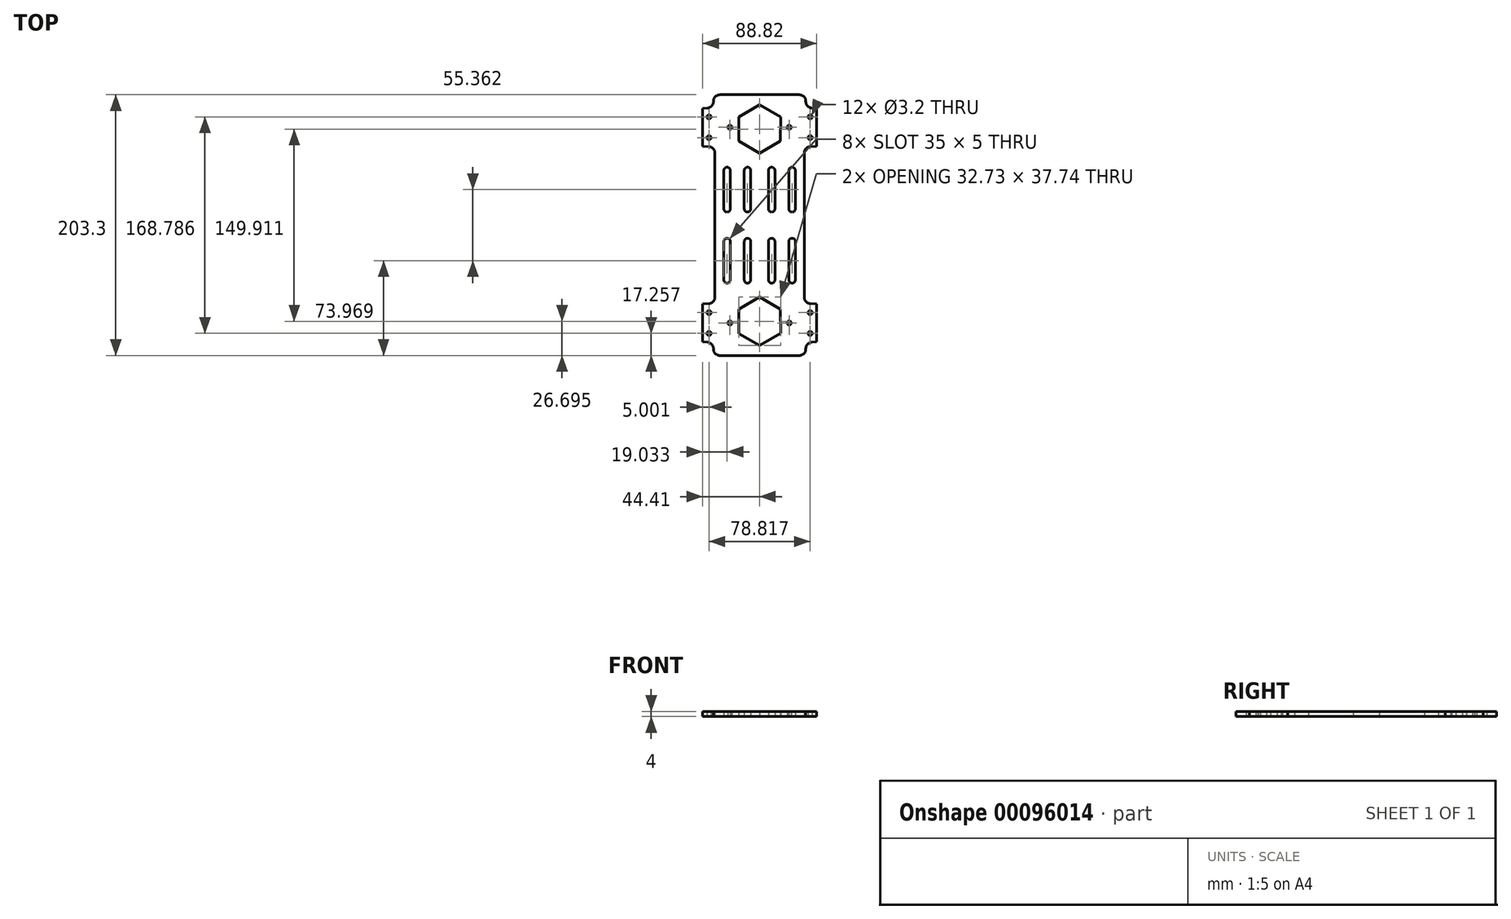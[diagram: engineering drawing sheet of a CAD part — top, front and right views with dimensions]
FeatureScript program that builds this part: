
annotation { "Feature Type Name" : "Feature", "Feature Type Description" : "" }
export const myFeature = defineFeature(function(context is Context, id is Id, definition is map)
    precondition{}
    {
        {
            var Q0;
            Q0=qCreatedBy(makeId("Top.planeOp"),FACE);
            var sketch = newSketch(context, id + "F0", { "sketchPlane" : qUnion([Q0])});
            skCircle(sketch, "E0", {"center": v(-39.4, -84.4) * mm, "radius": 1.6 * mm});
            skCircle(sketch, "E1", {"center": v(-39.4, -68.2) * mm, "radius": 1.6 * mm});
            skCircle(sketch, "E2", {"center": v(-23.11, -76.3) * mm, "radius": 1.6 * mm});
            skLineSegment(sketch, "E3", {"start": v(-39.4, -84.4) * mm, "end": v(-23.11, -76.3) * mm, "construction": true});
            skLineSegment(sketch, "E4", {"start": v(-23.11, -76.3) * mm, "end": v(-39.4, -68.2) * mm, "construction": true});
            skLineSegment(sketch, "E5", {"start": v(-39.4, -84.4) * mm, "end": v(-39.4, -68.2) * mm, "construction": true});
            skLineSegment(sketch, "E6", {"start": v(-44.4, -91.06) * mm, "end": v(-44.4, -61.53) * mm});
            skLineSegment(sketch, "E7", {"start": v(-44.4, -61.53) * mm, "end": v(-39.45, -61.18) * mm});
            skLineSegment(sketch, "E8", {"start": v(-34.8, -56.2) * mm, "end": v(-34.8, 0) * mm});
            skLineSegment(sketch, "E9.MirrorCS", {"start": v(-44.4, -91.06) * mm, "end": v(-40.65, -91.32) * mm});
            skPoint(sketch, "E10.visualSharp", {"position": v(-34.8, -60.85) * mm});
            skArc(sketch, "E10.filletArc", {"start": v(-39.45, -61.18) * mm, "mid": v(-36.14, -59.6) * mm, "end": v(-34.8, -56.2) * mm});
            skLineSegment(sketch, "E11", {"start": v(-36, -96.31) * mm, "end": v(-36, -96.65) * mm});
            skLineSegment(sketch, "E12", {"start": v(-31, -101.65) * mm, "end": v(0, -101.65) * mm});
            skPoint(sketch, "E13.visualSharp", {"position": v(-36, -101.65) * mm});
            skArc(sketch, "E13.filletArc", {"start": v(-36, -96.65) * mm, "mid": v(-34.54, -100.18) * mm, "end": v(-31, -101.65) * mm});
            skPoint(sketch, "E14.visualSharp", {"position": v(-36, -91.65) * mm});
            skArc(sketch, "E14.filletArc", {"start": v(-36, -96.31) * mm, "mid": v(-37.34, -92.9) * mm, "end": v(-40.65, -91.32) * mm});
            skCircle(sketch, "E15.MirrorC", {"center": v(23.11, -76.3) * mm, "radius": 1.6 * mm});
            skCircle(sketch, "E16.MirrorC", {"center": v(39.4, -68.2) * mm, "radius": 1.6 * mm});
            skCircle(sketch, "E17.MirrorC", {"center": v(39.4, -84.4) * mm, "radius": 1.6 * mm});
            skArc(sketch, "E18.MirrorCS", {"start": v(39.45, -61.18) * mm, "mid": v(36.14, -59.6) * mm, "end": v(34.8, -56.2) * mm});
            skLineSegment(sketch, "E19.MirrorCS", {"start": v(44.4, -91.06) * mm, "end": v(40.65, -91.32) * mm});
            skLineSegment(sketch, "E20.MirrorCS", {"start": v(36, -96.31) * mm, "end": v(36, -96.65) * mm});
            skArc(sketch, "E21.MirrorCS", {"start": v(36, -96.31) * mm, "mid": v(37.34, -92.9) * mm, "end": v(40.65, -91.32) * mm});
            skArc(sketch, "E22.MirrorCS", {"start": v(36, -96.65) * mm, "mid": v(34.54, -100.18) * mm, "end": v(31, -101.65) * mm});
            skLineSegment(sketch, "E23.MirrorCS", {"start": v(44.4, -61.53) * mm, "end": v(39.45, -61.18) * mm});
            skLineSegment(sketch, "E24.MirrorCS", {"start": v(39.4, -84.4) * mm, "end": v(39.4, -68.2) * mm, "construction": true});
            skLineSegment(sketch, "E25.MirrorCS", {"start": v(39.4, -84.4) * mm, "end": v(23.11, -76.3) * mm, "construction": true});
            skPoint(sketch, "E26.MirrorP", {"position": v(36, -101.65) * mm});
            skLineSegment(sketch, "E27.MirrorCS", {"start": v(23.11, -76.3) * mm, "end": v(39.4, -68.2) * mm, "construction": true});
            skLineSegment(sketch, "E28.MirrorCS", {"start": v(31, -101.65) * mm, "end": v(0, -101.65) * mm});
            skLineSegment(sketch, "E29.MirrorCS", {"start": v(34.8, -56.2) * mm, "end": v(34.8, 0) * mm});
            skPoint(sketch, "E30.MirrorP", {"position": v(36, -91.65) * mm});
            skPoint(sketch, "E31.MirrorP", {"position": v(34.8, -60.85) * mm});
            skCircle(sketch, "E32.MirrorC", {"center": v(-23.11, 76.3) * mm, "radius": 1.6 * mm});
            skCircle(sketch, "E33.MirrorC", {"center": v(-39.4, 84.4) * mm, "radius": 1.6 * mm});
            skCircle(sketch, "E34.MirrorC", {"center": v(-39.4, 68.2) * mm, "radius": 1.6 * mm});
            skArc(sketch, "E35.MirrorCS", {"start": v(-36, 96.31) * mm, "mid": v(-37.34, 92.9) * mm, "end": v(-40.65, 91.32) * mm});
            skLineSegment(sketch, "E36.MirrorCS", {"start": v(-44.4, 61.53) * mm, "end": v(-39.45, 61.18) * mm});
            skArc(sketch, "E37.MirrorCS", {"start": v(36, 96.65) * mm, "mid": v(34.54, 100.18) * mm, "end": v(31, 101.65) * mm});
            skCircle(sketch, "E38.MirrorC", {"center": v(39.4, 68.2) * mm, "radius": 1.6 * mm});
            skLineSegment(sketch, "E39.MirrorCS", {"start": v(36, 96.31) * mm, "end": v(36, 96.65) * mm});
            skArc(sketch, "E40.MirrorCS", {"start": v(-36, 96.65) * mm, "mid": v(-34.54, 100.18) * mm, "end": v(-31, 101.65) * mm});
            skArc(sketch, "E41.MirrorCS", {"start": v(36, 96.31) * mm, "mid": v(37.34, 92.9) * mm, "end": v(40.65, 91.32) * mm});
            skArc(sketch, "E42.MirrorCS", {"start": v(-39.45, 61.18) * mm, "mid": v(-36.14, 59.6) * mm, "end": v(-34.8, 56.2) * mm});
            skLineSegment(sketch, "E43.MirrorCS", {"start": v(-44.4, 91.06) * mm, "end": v(-40.65, 91.32) * mm});
            skCircle(sketch, "E44.MirrorC", {"center": v(23.11, 76.3) * mm, "radius": 1.6 * mm});
            skLineSegment(sketch, "E45.MirrorCS", {"start": v(-36, 96.31) * mm, "end": v(-36, 96.65) * mm});
            skCircle(sketch, "E46.MirrorC", {"center": v(39.4, 84.4) * mm, "radius": 1.6 * mm});
            skLineSegment(sketch, "E47.MirrorCS", {"start": v(44.4, 91.06) * mm, "end": v(40.65, 91.32) * mm});
            skArc(sketch, "E48.MirrorCS", {"start": v(39.45, 61.18) * mm, "mid": v(36.14, 59.6) * mm, "end": v(34.8, 56.2) * mm});
            skLineSegment(sketch, "E49.MirrorCS", {"start": v(44.4, 61.53) * mm, "end": v(39.45, 61.18) * mm});
            skLineSegment(sketch, "E50.MirrorCS", {"start": v(-39.4, 84.4) * mm, "end": v(-39.4, 68.2) * mm, "construction": true});
            skPoint(sketch, "E51.MirrorP", {"position": v(-34.8, 60.85) * mm});
            skLineSegment(sketch, "E52.MirrorCS", {"start": v(-39.4, 84.4) * mm, "end": v(-23.11, 76.3) * mm, "construction": true});
            skLineSegment(sketch, "E53.MirrorCS", {"start": v(-23.11, 76.3) * mm, "end": v(-39.4, 68.2) * mm, "construction": true});
            skPoint(sketch, "E54.MirrorP", {"position": v(34.8, 60.85) * mm});
            skLineSegment(sketch, "E55.MirrorCS", {"start": v(39.4, 84.4) * mm, "end": v(39.4, 68.2) * mm, "construction": true});
            skPoint(sketch, "E56.MirrorP", {"position": v(-36, 91.65) * mm});
            skLineSegment(sketch, "E57.MirrorCS", {"start": v(-34.8, 56.2) * mm, "end": v(-34.8, 0) * mm});
            skPoint(sketch, "E58.MirrorP", {"position": v(36, 101.65) * mm});
            skLineSegment(sketch, "E59.MirrorCS", {"start": v(23.11, 76.3) * mm, "end": v(39.4, 68.2) * mm, "construction": true});
            skPoint(sketch, "E60.MirrorP", {"position": v(-36, 101.65) * mm});
            skLineSegment(sketch, "E61.MirrorCS", {"start": v(34.8, 56.2) * mm, "end": v(34.8, 0) * mm});
            skLineSegment(sketch, "E62.MirrorCS", {"start": v(31, 101.65) * mm, "end": v(0, 101.65) * mm});
            skLineSegment(sketch, "E63.MirrorCS", {"start": v(39.4, 84.4) * mm, "end": v(23.11, 76.3) * mm, "construction": true});
            skPoint(sketch, "E64.MirrorP", {"position": v(36, 91.65) * mm});
            skLineSegment(sketch, "E65.MirrorCS", {"start": v(-31, 101.65) * mm, "end": v(0, 101.65) * mm});
            skLineSegment(sketch, "E66", {"start": v(-34.8, 0) * mm, "end": v(0, 0) * mm, "construction": true});
            skPoint(sketch, "E67.cCircle.centerSnap1", {"position": v(-17.4, 0) * mm});
            skLineSegment(sketch, "E68.bottom", {"start": v(25.38, -45.18) * mm, "end": v(25.38, -45.18) * mm});
            skLineSegment(sketch, "E68.top", {"start": v(25.38, -10.18) * mm, "end": v(25.38, -10.18) * mm});
            skLineSegment(sketch, "E68.left", {"start": v(22.88, -42.68) * mm, "end": v(22.88, -12.68) * mm});
            skLineSegment(sketch, "E68.right", {"start": v(27.88, -42.68) * mm, "end": v(27.88, -12.68) * mm});
            skPoint(sketch, "E68.middle.positionSnap0", {"position": v(34.8, -28.1) * mm});
            skPoint(sketch, "E68.centerSnap0", {"position": v(34.8, -28.1) * mm});
            skPoint(sketch, "E69.visualSharp", {"position": v(22.88, -10.18) * mm});
            skArc(sketch, "E69.filletArc", {"start": v(25.38, -10.18) * mm, "mid": v(23.6, -10.91) * mm, "end": v(22.88, -12.68) * mm});
            skPoint(sketch, "E70.visualSharp", {"position": v(27.88, -10.18) * mm});
            skArc(sketch, "E70.filletArc", {"start": v(27.88, -12.68) * mm, "mid": v(27.15, -10.91) * mm, "end": v(25.38, -10.18) * mm});
            skPoint(sketch, "E71.visualSharp", {"position": v(27.88, -45.18) * mm});
            skArc(sketch, "E71.filletArc", {"start": v(25.38, -45.18) * mm, "mid": v(27.15, -44.45) * mm, "end": v(27.88, -42.68) * mm});
            skPoint(sketch, "E72.visualSharp", {"position": v(22.88, -45.18) * mm});
            skArc(sketch, "E72.filletArc", {"start": v(22.88, -42.68) * mm, "mid": v(23.6, -44.45) * mm, "end": v(25.38, -45.18) * mm});
            skLineSegment(sketch, "E73", {"start": v(34.8, 0) * mm, "end": v(0, 0) * mm, "construction": true});
            skLineSegment(sketch, "E74", {"start": v(17.4, 0) * mm, "end": v(17.4, -61.5) * mm, "construction": true});
            skLineSegment(sketch, "E75.MirrorCS", {"start": v(9.42, -45.18) * mm, "end": v(9.42, -45.18) * mm});
            skLineSegment(sketch, "E76.MirrorCS", {"start": v(9.42, -10.18) * mm, "end": v(9.42, -10.18) * mm});
            skArc(sketch, "E77.MirrorCS", {"start": v(9.42, -10.18) * mm, "mid": v(11.19, -10.91) * mm, "end": v(11.92, -12.68) * mm});
            skArc(sketch, "E78.MirrorCS", {"start": v(11.92, -42.68) * mm, "mid": v(11.19, -44.45) * mm, "end": v(9.42, -45.18) * mm});
            skArc(sketch, "E79.MirrorCS", {"start": v(9.42, -45.18) * mm, "mid": v(7.65, -44.45) * mm, "end": v(6.92, -42.68) * mm});
            skArc(sketch, "E80.MirrorCS", {"start": v(6.92, -12.68) * mm, "mid": v(7.65, -10.91) * mm, "end": v(9.42, -10.18) * mm});
            skPoint(sketch, "E81.MirrorP", {"position": v(11.92, -10.18) * mm});
            skPoint(sketch, "E82.MirrorP", {"position": v(6.92, -10.18) * mm});
            skLineSegment(sketch, "E83.MirrorCS", {"start": v(11.92, -42.68) * mm, "end": v(11.92, -12.68) * mm});
            skPoint(sketch, "E84.MirrorP", {"position": v(6.92, -45.18) * mm});
            skPoint(sketch, "E85.MirrorP", {"position": v(11.92, -45.18) * mm});
            skLineSegment(sketch, "E86.MirrorCS", {"start": v(6.92, -42.68) * mm, "end": v(6.92, -12.68) * mm});
            skLineSegment(sketch, "E87", {"start": v(0, 0) * mm, "end": v(0, -74.96) * mm, "construction": true});
            skLineSegment(sketch, "E88.MirrorCS", {"start": v(-9.42, -10.18) * mm, "end": v(-9.42, -10.18) * mm});
            skLineSegment(sketch, "E89.MirrorCS", {"start": v(-25.38, -10.18) * mm, "end": v(-25.38, -10.18) * mm});
            skLineSegment(sketch, "E90.MirrorCS", {"start": v(-9.42, -45.18) * mm, "end": v(-9.42, -45.18) * mm});
            skLineSegment(sketch, "E91.MirrorCS", {"start": v(-25.38, -45.18) * mm, "end": v(-25.38, -45.18) * mm});
            skArc(sketch, "E92.MirrorCS", {"start": v(-25.38, -45.18) * mm, "mid": v(-27.15, -44.45) * mm, "end": v(-27.88, -42.68) * mm});
            skArc(sketch, "E93.MirrorCS", {"start": v(-6.92, -12.68) * mm, "mid": v(-7.65, -10.91) * mm, "end": v(-9.42, -10.18) * mm});
            skArc(sketch, "E94.MirrorCS", {"start": v(-22.88, -42.68) * mm, "mid": v(-23.6, -44.45) * mm, "end": v(-25.38, -45.18) * mm});
            skArc(sketch, "E95.MirrorCS", {"start": v(-9.42, -45.18) * mm, "mid": v(-7.65, -44.45) * mm, "end": v(-6.92, -42.68) * mm});
            skArc(sketch, "E96.MirrorCS", {"start": v(-27.88, -12.68) * mm, "mid": v(-27.15, -10.91) * mm, "end": v(-25.38, -10.18) * mm});
            skArc(sketch, "E97.MirrorCS", {"start": v(-11.92, -42.68) * mm, "mid": v(-11.19, -44.45) * mm, "end": v(-9.42, -45.18) * mm});
            skArc(sketch, "E98.MirrorCS", {"start": v(-25.38, -10.18) * mm, "mid": v(-23.6, -10.91) * mm, "end": v(-22.88, -12.68) * mm});
            skArc(sketch, "E99.MirrorCS", {"start": v(-9.42, -10.18) * mm, "mid": v(-11.19, -10.91) * mm, "end": v(-11.92, -12.68) * mm});
            skPoint(sketch, "E100.MirrorP", {"position": v(-11.92, -45.18) * mm});
            skPoint(sketch, "E101.MirrorP", {"position": v(-6.92, -45.18) * mm});
            skLineSegment(sketch, "E102.MirrorCS", {"start": v(-6.92, -42.68) * mm, "end": v(-6.92, -12.68) * mm});
            skPoint(sketch, "E103.MirrorP", {"position": v(-22.88, -10.18) * mm});
            skPoint(sketch, "E104.MirrorP", {"position": v(-22.88, -45.18) * mm});
            skPoint(sketch, "E105.MirrorP", {"position": v(-27.88, -10.18) * mm});
            skLineSegment(sketch, "E106.MirrorCS", {"start": v(-22.88, -42.68) * mm, "end": v(-22.88, -12.68) * mm});
            skPoint(sketch, "E107.MirrorP", {"position": v(-6.92, -10.18) * mm});
            skLineSegment(sketch, "E108.MirrorCS", {"start": v(-11.92, -42.68) * mm, "end": v(-11.92, -12.68) * mm});
            skPoint(sketch, "E109.MirrorP", {"position": v(-11.92, -10.18) * mm});
            skLineSegment(sketch, "E110.MirrorCS", {"start": v(-27.88, -42.68) * mm, "end": v(-27.88, -12.68) * mm});
            skPoint(sketch, "E111.MirrorP", {"position": v(-27.88, -45.18) * mm});
            skLineSegment(sketch, "E112.MirrorCS", {"start": v(-25.38, 45.18) * mm, "end": v(-25.38, 45.18) * mm});
            skLineSegment(sketch, "E113.MirrorCS", {"start": v(-25.38, 10.18) * mm, "end": v(-25.38, 10.18) * mm});
            skArc(sketch, "E114.MirrorCS", {"start": v(-25.38, 10.18) * mm, "mid": v(-23.6, 10.91) * mm, "end": v(-22.88, 12.68) * mm});
            skArc(sketch, "E115.MirrorCS", {"start": v(-27.88, 12.68) * mm, "mid": v(-27.15, 10.91) * mm, "end": v(-25.38, 10.18) * mm});
            skArc(sketch, "E116.MirrorCS", {"start": v(-25.38, 45.18) * mm, "mid": v(-27.15, 44.45) * mm, "end": v(-27.88, 42.68) * mm});
            skArc(sketch, "E117.MirrorCS", {"start": v(-22.88, 42.68) * mm, "mid": v(-23.6, 44.45) * mm, "end": v(-25.38, 45.18) * mm});
            skLineSegment(sketch, "E118.MirrorCS", {"start": v(9.42, 10.18) * mm, "end": v(9.42, 10.18) * mm});
            skLineSegment(sketch, "E119.MirrorCS", {"start": v(25.38, 10.18) * mm, "end": v(25.38, 10.18) * mm});
            skLineSegment(sketch, "E120.MirrorCS", {"start": v(9.42, 45.18) * mm, "end": v(9.42, 45.18) * mm});
            skLineSegment(sketch, "E121.MirrorCS", {"start": v(-9.42, 10.18) * mm, "end": v(-9.42, 10.18) * mm});
            skLineSegment(sketch, "E122.MirrorCS", {"start": v(25.38, 45.18) * mm, "end": v(25.38, 45.18) * mm});
            skArc(sketch, "E123.MirrorCS", {"start": v(25.38, 45.18) * mm, "mid": v(27.15, 44.45) * mm, "end": v(27.88, 42.68) * mm});
            skArc(sketch, "E124.MirrorCS", {"start": v(6.92, 12.68) * mm, "mid": v(7.65, 10.91) * mm, "end": v(9.42, 10.18) * mm});
            skArc(sketch, "E125.MirrorCS", {"start": v(-6.92, 12.68) * mm, "mid": v(-7.65, 10.91) * mm, "end": v(-9.42, 10.18) * mm});
            skArc(sketch, "E126.MirrorCS", {"start": v(-9.42, 45.18) * mm, "mid": v(-7.65, 44.45) * mm, "end": v(-6.92, 42.68) * mm});
            skArc(sketch, "E127.MirrorCS", {"start": v(9.42, 45.18) * mm, "mid": v(7.65, 44.45) * mm, "end": v(6.92, 42.68) * mm});
            skArc(sketch, "E128.MirrorCS", {"start": v(27.88, 12.68) * mm, "mid": v(27.15, 10.91) * mm, "end": v(25.38, 10.18) * mm});
            skLineSegment(sketch, "E129.MirrorCS", {"start": v(-9.42, 45.18) * mm, "end": v(-9.42, 45.18) * mm});
            skArc(sketch, "E130.MirrorCS", {"start": v(25.38, 10.18) * mm, "mid": v(23.6, 10.91) * mm, "end": v(22.88, 12.68) * mm});
            skArc(sketch, "E131.MirrorCS", {"start": v(11.92, 42.68) * mm, "mid": v(11.19, 44.45) * mm, "end": v(9.42, 45.18) * mm});
            skArc(sketch, "E132.MirrorCS", {"start": v(-11.92, 42.68) * mm, "mid": v(-11.19, 44.45) * mm, "end": v(-9.42, 45.18) * mm});
            skArc(sketch, "E133.MirrorCS", {"start": v(9.42, 10.18) * mm, "mid": v(11.19, 10.91) * mm, "end": v(11.92, 12.68) * mm});
            skArc(sketch, "E134.MirrorCS", {"start": v(22.88, 42.68) * mm, "mid": v(23.6, 44.45) * mm, "end": v(25.38, 45.18) * mm});
            skArc(sketch, "E135.MirrorCS", {"start": v(-9.42, 10.18) * mm, "mid": v(-11.19, 10.91) * mm, "end": v(-11.92, 12.68) * mm});
            skPoint(sketch, "E136.MirrorP", {"position": v(34.8, 28.1) * mm});
            skPoint(sketch, "E137.MirrorP", {"position": v(-11.92, 10.18) * mm});
            skLineSegment(sketch, "E138.MirrorCS", {"start": v(-6.92, 42.68) * mm, "end": v(-6.92, 12.68) * mm});
            skLineSegment(sketch, "E139.MirrorCS", {"start": v(22.88, 42.68) * mm, "end": v(22.88, 12.68) * mm});
            skPoint(sketch, "E140.MirrorP", {"position": v(6.92, 45.18) * mm});
            skPoint(sketch, "E141.MirrorP", {"position": v(27.88, 10.18) * mm});
            skPoint(sketch, "E142.MirrorP", {"position": v(-6.92, 45.18) * mm});
            skPoint(sketch, "E143.MirrorP", {"position": v(22.88, 10.18) * mm});
            skPoint(sketch, "E144.MirrorP", {"position": v(-22.88, 10.18) * mm});
            skPoint(sketch, "E145.MirrorP", {"position": v(22.88, 45.18) * mm});
            skPoint(sketch, "E146.MirrorP", {"position": v(-6.92, 10.18) * mm});
            skLineSegment(sketch, "E147.MirrorCS", {"start": v(-11.92, 42.68) * mm, "end": v(-11.92, 12.68) * mm});
            skPoint(sketch, "E148.MirrorP", {"position": v(6.92, 10.18) * mm});
            skLineSegment(sketch, "E149.MirrorCS", {"start": v(-27.88, 42.68) * mm, "end": v(-27.88, 12.68) * mm});
            skPoint(sketch, "E150.MirrorP", {"position": v(-27.88, 10.18) * mm});
            skPoint(sketch, "E151.MirrorP", {"position": v(11.92, 10.18) * mm});
            skLineSegment(sketch, "E152.MirrorCS", {"start": v(27.88, 42.68) * mm, "end": v(27.88, 12.68) * mm});
            skPoint(sketch, "E153.MirrorP", {"position": v(27.88, 45.18) * mm});
            skPoint(sketch, "E154.MirrorP", {"position": v(-22.88, 45.18) * mm});
            skPoint(sketch, "E155.MirrorP", {"position": v(-27.88, 45.18) * mm});
            skLineSegment(sketch, "E156.MirrorCS", {"start": v(-22.88, 42.68) * mm, "end": v(-22.88, 12.68) * mm});
            skPoint(sketch, "E157.MirrorP", {"position": v(11.92, 45.18) * mm});
            skLineSegment(sketch, "E158.MirrorCS", {"start": v(11.92, 42.68) * mm, "end": v(11.92, 12.68) * mm});
            skPoint(sketch, "E159.MirrorP", {"position": v(-11.92, 45.18) * mm});
            skLineSegment(sketch, "E160.MirrorCS", {"start": v(6.92, 42.68) * mm, "end": v(6.92, 12.68) * mm});
            skCircle(sketch, "E161.cCircle", {"center": v(0, -74.96) * mm, "radius": 16.34 * mm, "construction": true});
            skLineSegment(sketch, "E161.0", {"start": v(16.36, -84.35) * mm, "end": v(0.05, -93.82) * mm});
            skLineSegment(sketch, "E161.1", {"start": v(0.05, -93.82) * mm, "end": v(-16.32, -84.43) * mm});
            skLineSegment(sketch, "E161.2", {"start": v(-16.32, -84.43) * mm, "end": v(-16.36, -65.56) * mm});
            skLineSegment(sketch, "E161.3", {"start": v(-16.36, -65.56) * mm, "end": v(-0.05, -56.09) * mm});
            skLineSegment(sketch, "E161.4", {"start": v(-0.05, -56.09) * mm, "end": v(16.32, -65.48) * mm});
            skLineSegment(sketch, "E161.5", {"start": v(16.32, -65.48) * mm, "end": v(16.36, -84.35) * mm});
            skPoint(sketch, "E161.0.midPoint", {"position": v(8.2, -89.09) * mm});
            skLineSegment(sketch, "E162.MirrorCS", {"start": v(-16.36, 65.56) * mm, "end": v(-0.05, 56.09) * mm});
            skLineSegment(sketch, "E163.MirrorCS", {"start": v(16.36, 84.35) * mm, "end": v(0.05, 93.82) * mm});
            skCircle(sketch, "E164.MirrorC", {"center": v(0, 74.96) * mm, "radius": 16.34 * mm, "construction": true});
            skPoint(sketch, "E165.MirrorP", {"position": v(8.2, 89.09) * mm});
            skLineSegment(sketch, "E166.MirrorCS", {"start": v(-16.32, 84.43) * mm, "end": v(-16.36, 65.56) * mm});
            skLineSegment(sketch, "E167.MirrorCS", {"start": v(16.32, 65.48) * mm, "end": v(16.36, 84.35) * mm});
            skLineSegment(sketch, "E168.MirrorCS", {"start": v(0.05, 93.82) * mm, "end": v(-16.32, 84.43) * mm});
            skLineSegment(sketch, "E169.MirrorCS", {"start": v(-0.05, 56.09) * mm, "end": v(16.32, 65.48) * mm});
            skLineSegment(sketch, "E170.MirrorCS", {"start": v(44.4, -91.06) * mm, "end": v(44.4, -61.53) * mm});
            skLineSegment(sketch, "E171.MirrorCS", {"start": v(-44.4, 91.06) * mm, "end": v(-44.4, 61.53) * mm});
            skLineSegment(sketch, "E172.MirrorCS", {"start": v(44.4, 91.06) * mm, "end": v(44.4, 61.53) * mm});
            skSolve(sketch);
        }
        {
            var Q0;
            Q0 = qSketchRegion(id + "F0", true);
            extrude(context, id + "F1", {"entities" : qUnion([Q0]), "depth" : 4 * mm});
        }
    });
